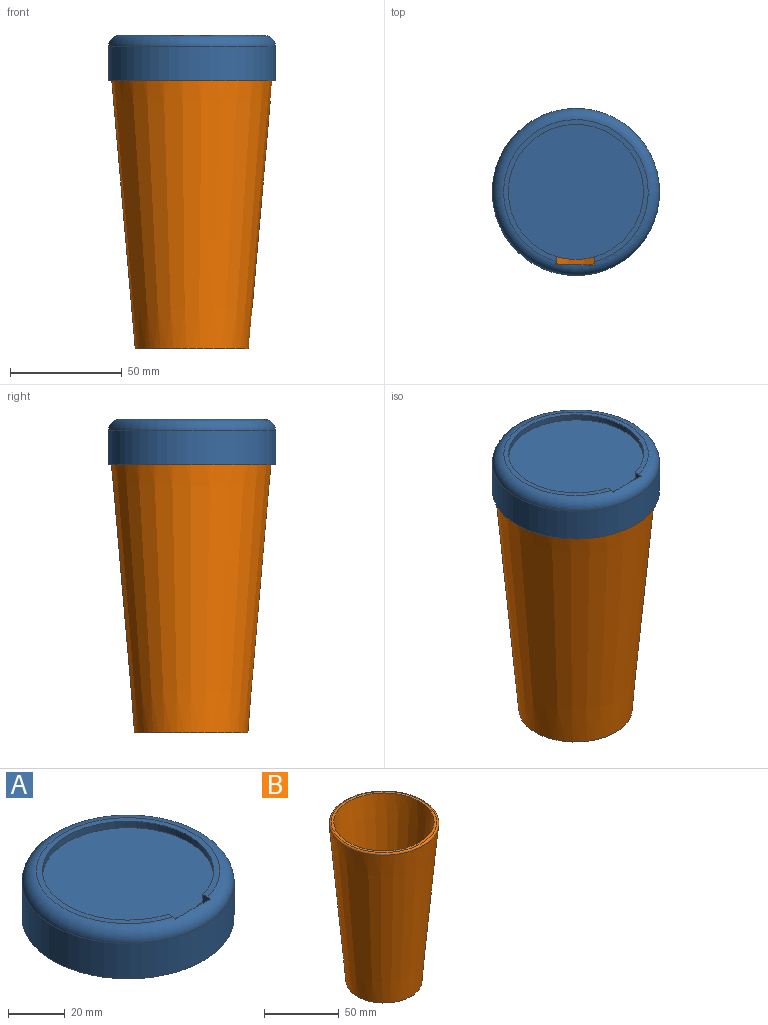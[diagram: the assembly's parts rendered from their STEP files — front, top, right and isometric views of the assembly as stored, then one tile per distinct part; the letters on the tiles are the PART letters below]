
ASSEMBLY  parts=2 mates=1
PART A: 12 faces, bbox 81.1x81.1x20.3 mm
  f0: plane 17.53x9.9mm, normal (0.01,1,0), area 172.6mm2, adj f1,f2,f9,f10
  f1: plane 9.92x3.68mm, normal (1,-0.07,0), area 36.3mm2, adj f0,f3,f4,f7,f9,f10
  f2: plane 9.92x3.67mm, normal (-1,-0.07,0), area 36.3mm2, adj f0,f3,f4,f7,f9,f10
  f3: cylinder r=30.25mm len=17.03mm, axis (0,0,1), area 122.8mm2, adj f1,f2,f8,f10
  f4: plane 64.77x63.64mm, normal (0,0,1), area 382.3mm2, adj f1,f2,f7,f9
  f5: plane 74.93x74.93mm, normal (0,0,-1), area 151.1mm2, adj f6,f11
  f6: cylinder r=37.46mm len=74.93mm, axis (0,0,-1), area 3587.5mm2, adj f5,f9
  f7: cylinder r=30.25mm len=60.51mm, axis (0,0,1), area 482.9mm2, adj f1,f2,f4,f8
  f8: plane 60.51x60.51mm, normal (0,0,1), area 2875.5mm2, adj f3,f7
  f9: torus R=32.38mm, axis (0,0,1), area 1773.4mm2, adj f0,f1,f2,f4,f6
  f10: plane 73.64x73.64mm, normal (0,0,-1), area 4209.1mm2, adj f0,f1,f2,f3,f11
  f11: cylinder r=36.82mm len=73.64mm, axis (0,0,-1), area 2409.1mm2, adj f5,f10
PART B: 8 faces, bbox 79.5x79.5x130.5 mm
  f0: plane 70.86x70.86mm, normal (0,0,1), area 406mm2, adj f6,f7
  f1: cone r=36.82mm half-angle=5deg, axis (0,0,1), area 25285.4mm2, adj f2,f7
  f2: plane 50.8x50.8mm, normal (0,0,-1), area 81.4mm2, adj f1,f3
  f3: cylinder r=24.88mm len=49.77mm, axis (0,0,-1), area 77.8mm2, adj f2,f4
  f4: plane 49.77x49.77mm, normal (0,0,-1), area 1945.4mm2, adj f3
  f5: plane 44.46x44.46mm, normal (0,0,1), area 1552.2mm2, adj f6
  f6: cone r=22.23mm half-angle=5deg, axis (0,0,1), area 22783.3mm2, adj f0,f5
  f7: torus R=35.43mm, axis (0,0,-1), area 479.8mm2, adj f0,f1
PLACE A t=(60.42,15.23,-39.93)mm
PLACE B t=(80.72,15.59,-83.75)mm
MATE cylindrical B.f1 <-> A.f10  axis (0,0,1) through (60.42,15.59,-29.52)mm
